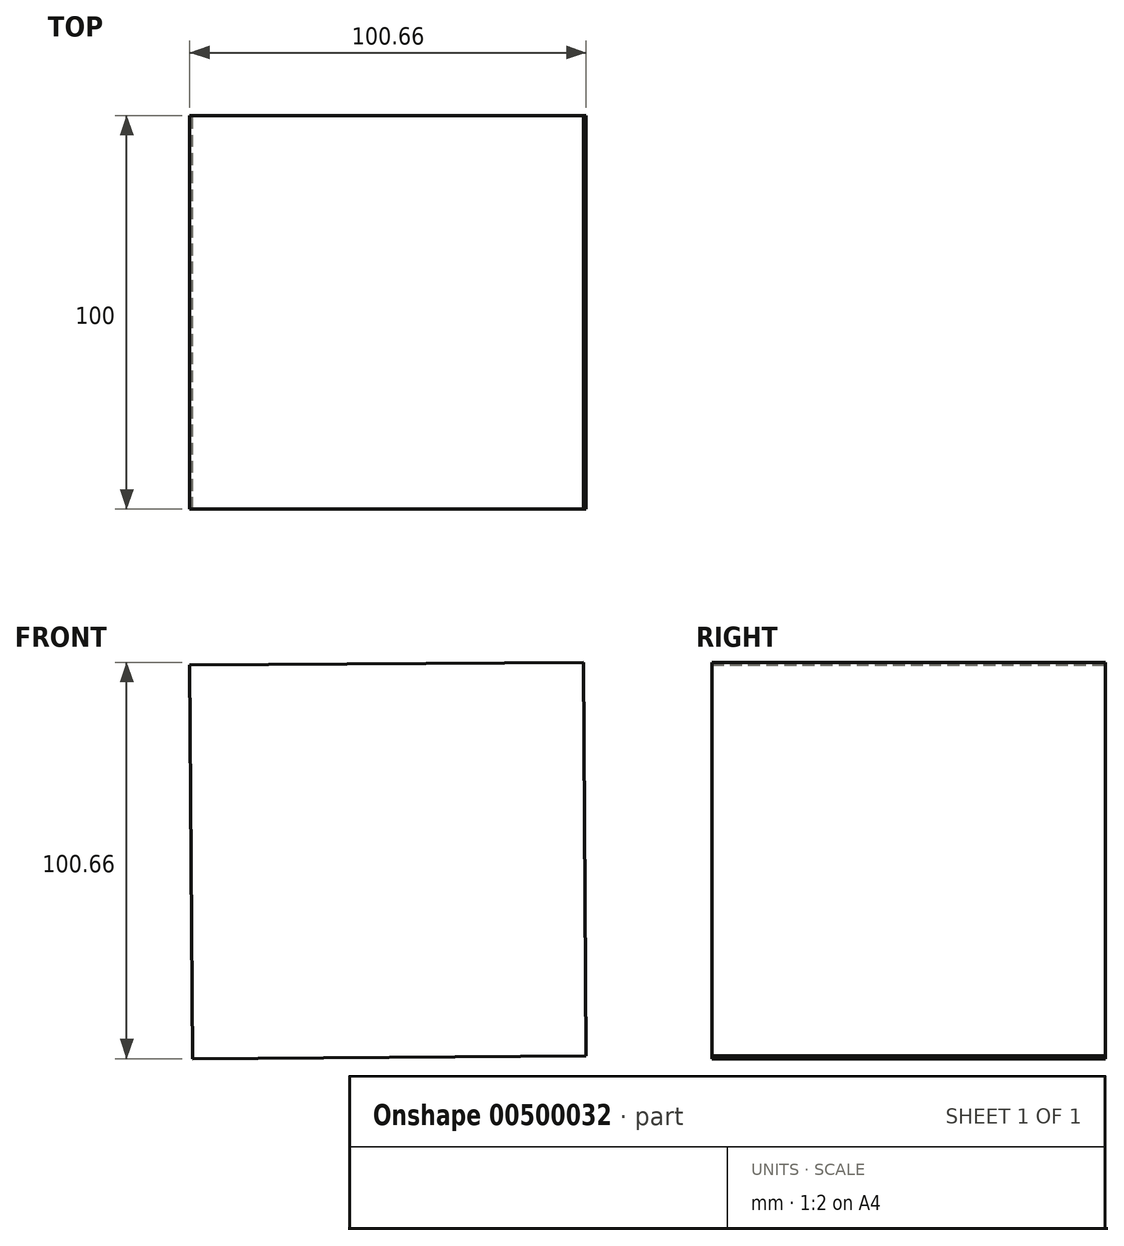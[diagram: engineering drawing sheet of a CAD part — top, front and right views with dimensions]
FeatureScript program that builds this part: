
annotation { "Feature Type Name" : "Feature", "Feature Type Description" : "" }
export const myFeature = defineFeature(function(context is Context, id is Id, definition is map)
    precondition{}
    {
        {
            var Q0;
            Q0=qCreatedBy(makeId("Front.planeOp"),FACE);
            var sketch = newSketch(context, id + "F0", { "sketchPlane" : qUnion([Q0])});
            skCircle(sketch, "E0.cCircle", {"center": v(0, 0) * mm, "radius": 70.71 * mm, "construction": true});
            skLineSegment(sketch, "E0.0", {"start": v(49.66, 50.33) * mm, "end": v(50.33, -49.66) * mm});
            skLineSegment(sketch, "E0.1", {"start": v(50.33, -49.66) * mm, "end": v(-49.66, -50.33) * mm});
            skLineSegment(sketch, "E0.2", {"start": v(-49.66, -50.33) * mm, "end": v(-50.33, 49.66) * mm});
            skLineSegment(sketch, "E0.3", {"start": v(-50.33, 49.66) * mm, "end": v(49.66, 50.33) * mm});
            skSolve(sketch);
        }
        {
            var Q0;
            Q0 = qSketchRegion(id + "F0", true);
            extrude(context, id + "F1", {"entities" : qUnion([Q0]), "endBound" : BoundingType.SYMMETRIC, "depth" : 100 * mm});
        }
    });
